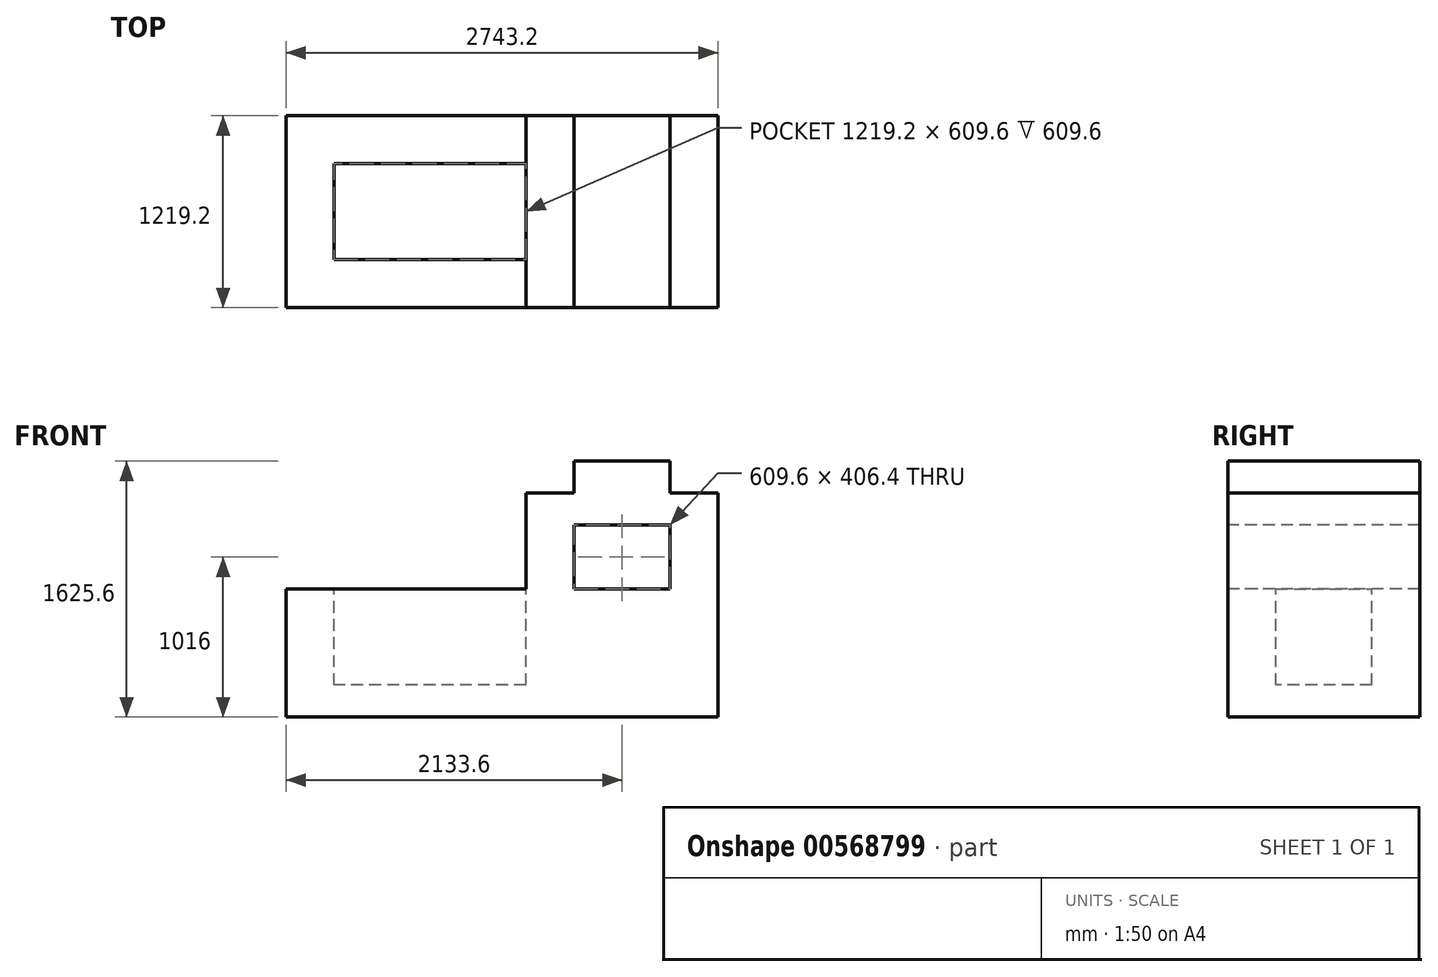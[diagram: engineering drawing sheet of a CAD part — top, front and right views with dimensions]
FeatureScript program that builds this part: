
annotation { "Feature Type Name" : "Feature", "Feature Type Description" : "" }
export const myFeature = defineFeature(function(context is Context, id is Id, definition is map)
    precondition{}
    {
        {
            var Q0;
            Q0=qCreatedBy(makeId("Front.planeOp"),FACE);
            var sketch = newSketch(context, id + "F0", { "sketchPlane" : qUnion([Q0])});
            skLineSegment(sketch, "E0.bottom", {"start": v(0, 0) * mm, "end": v(-2743.2, 0) * mm});
            skLineSegment(sketch, "E0.top", {"start": v(0, 1625.6) * mm, "end": v(-2743.2, 1625.6) * mm});
            skLineSegment(sketch, "E0.left", {"start": v(0, 0) * mm, "end": v(0, 1625.6) * mm});
            skLineSegment(sketch, "E0.right", {"start": v(-2743.2, 0) * mm, "end": v(-2743.2, 1625.6) * mm});
            skSolve(sketch);
        }
        {
            var Q0;
            Q0=makeQuery(id+"F0.imprint","IMPRINT",FACE,{"disambiguationData":[TD([[makeQuery(id+"F0.imprint","IMPRINT",EDGE,{"derivedFrom":sQuery(id+"F0.wireOp",EDGE,"E0.bottom")}),-1.0]])]});
            extrude(context, id + "F1", {"entities" : qUnion([Q0]), "depth" : 1219.2 * mm, "offsetDistance" : 25.4 * mm});
        }
        {
            var Q0;
            Q0=makeQuery(id+"F1.opExtrude","CAP_FACE",FACE,{"disambiguationData":[OSD([sQuery(id+"F0.wireOp",EDGE,"E0.bottom"),sQuery(id+"F0.wireOp",EDGE,"E0.top"),sQuery(id+"F0.wireOp",EDGE,"E0.left"),sQuery(id+"F0.wireOp",EDGE,"E0.right")])],"isStart":false});
            var sketch = newSketch(context, id + "F2", { "sketchPlane" : qUnion([Q0])});
            skLineSegment(sketch, "E1.bottom", {"start": v(-2743.2, 1625.6) * mm, "end": v(-1219.2, 1625.6) * mm});
            skLineSegment(sketch, "E1.top", {"start": v(-2743.2, 812.8) * mm, "end": v(-1219.2, 812.8) * mm});
            skLineSegment(sketch, "E1.left", {"start": v(-2743.2, 1625.6) * mm, "end": v(-2743.2, 812.8) * mm});
            skLineSegment(sketch, "E1.right", {"start": v(-1219.2, 1625.6) * mm, "end": v(-1219.2, 812.8) * mm});
            skSolve(sketch);
        }
        {
            var Q0;
            Q0 = qSketchRegion(id + "F2", true);
            var Q1;
            Q1=makeQuery(id+"F2.imprint","IMPRINT",FACE,{"disambiguationData":[TD([[makeQuery(id+"F2.imprint","IMPRINT",EDGE,{"derivedFrom":sQuery(id+"F2.wireOp",EDGE,"E1.bottom")}),1.0]])]});
            extrude(context, id + "F3", {"entities" : qUnion([Q0, Q1]), "operationType" : NewBodyOperationType.REMOVE, "endBound" : BoundingType.THROUGH_ALL, "oppositeDirection" : true, "depth" : 25.4 * mm, "offsetDistance" : 25.4 * mm});
        }
        {
            var Q0;
            Q0=makeQuery(id+"F1.opExtrude","CAP_FACE",FACE,{"disambiguationData":[OSD([sQuery(id+"F0.wireOp",EDGE,"E0.bottom"),sQuery(id+"F0.wireOp",EDGE,"E0.top"),sQuery(id+"F0.wireOp",EDGE,"E0.left"),sQuery(id+"F0.wireOp",EDGE,"E0.right")])],"isStart":false});
            var sketch = newSketch(context, id + "F4", { "sketchPlane" : qUnion([Q0])});
            skLineSegment(sketch, "E2.bottom", {"start": v(-1219.2, 1625.6) * mm, "end": v(-914.4, 1625.6) * mm});
            skLineSegment(sketch, "E2.top", {"start": v(-1219.2, 1422.4) * mm, "end": v(-914.4, 1422.4) * mm});
            skLineSegment(sketch, "E2.left", {"start": v(-1219.2, 1625.6) * mm, "end": v(-1219.2, 1422.4) * mm});
            skLineSegment(sketch, "E2.right", {"start": v(-914.4, 1625.6) * mm, "end": v(-914.4, 1422.4) * mm});
            skSolve(sketch);
        }
        {
            var Q0;
            Q0 = qSketchRegion(id + "F4", true);
            extrude(context, id + "F5", {"entities" : qUnion([Q0]), "operationType" : NewBodyOperationType.REMOVE, "endBound" : BoundingType.THROUGH_ALL, "oppositeDirection" : true, "depth" : 25.4 * mm, "offsetDistance" : 25.4 * mm});
        }
        {
            var Q0;
            Q0=makeQuery(id+"F1.opExtrude","CAP_FACE",FACE,{"disambiguationData":[OSD([sQuery(id+"F0.wireOp",EDGE,"E0.bottom"),sQuery(id+"F0.wireOp",EDGE,"E0.top"),sQuery(id+"F0.wireOp",EDGE,"E0.left"),sQuery(id+"F0.wireOp",EDGE,"E0.right")])],"isStart":false});
            var sketch = newSketch(context, id + "F6", { "sketchPlane" : qUnion([Q0])});
            skLineSegment(sketch, "E3.bottom", {"start": v(0, 1625.6) * mm, "end": v(-304.8, 1625.6) * mm});
            skLineSegment(sketch, "E3.top", {"start": v(0, 1422.4) * mm, "end": v(-304.8, 1422.4) * mm});
            skLineSegment(sketch, "E3.left", {"start": v(0, 1625.6) * mm, "end": v(0, 1422.4) * mm});
            skLineSegment(sketch, "E3.right", {"start": v(-304.8, 1625.6) * mm, "end": v(-304.8, 1422.4) * mm});
            skSolve(sketch);
        }
        {
            var Q0;
            Q0 = qSketchRegion(id + "F6", true);
            extrude(context, id + "F7", {"entities" : qUnion([Q0]), "operationType" : NewBodyOperationType.REMOVE, "endBound" : BoundingType.THROUGH_ALL, "oppositeDirection" : true, "depth" : 25.4 * mm, "offsetDistance" : 25.4 * mm});
        }
        {
            var Q0;
            Q0=makeQuery(id+"F1.opExtrude","CAP_FACE",FACE,{"disambiguationData":[OSD([sQuery(id+"F0.wireOp",EDGE,"E0.bottom"),sQuery(id+"F0.wireOp",EDGE,"E0.top"),sQuery(id+"F0.wireOp",EDGE,"E0.left"),sQuery(id+"F0.wireOp",EDGE,"E0.right")])],"isStart":false});
            var sketch = newSketch(context, id + "F8", { "sketchPlane" : qUnion([Q0])});
            skLineSegment(sketch, "E4", {"start": v(-1219.2, 1422.4) * mm, "end": v(-1219.2, 1219.2) * mm});
            skLineSegment(sketch, "E5.bottom", {"start": v(-914.4, 1219.2) * mm, "end": v(-304.8, 1219.2) * mm});
            skLineSegment(sketch, "E5.top", {"start": v(-914.4, 812.8) * mm, "end": v(-304.8, 812.8) * mm});
            skLineSegment(sketch, "E5.left", {"start": v(-914.4, 1219.2) * mm, "end": v(-914.4, 812.8) * mm});
            skLineSegment(sketch, "E5.right", {"start": v(-304.8, 1219.2) * mm, "end": v(-304.8, 812.8) * mm});
            skSolve(sketch);
        }
        {
            var Q0;
            Q0=makeQuery(id+"F8.imprint","IMPRINT",FACE,{"disambiguationData":[TD([[makeQuery(id+"F8.imprint","IMPRINT",EDGE,{"derivedFrom":sQuery(id+"F8.wireOp",EDGE,"E5.bottom")}),-1.0]])]});
            extrude(context, id + "F9", {"entities" : qUnion([Q0]), "operationType" : NewBodyOperationType.REMOVE, "endBound" : BoundingType.THROUGH_ALL, "oppositeDirection" : true, "depth" : 25.4 * mm, "offsetDistance" : 25.4 * mm});
        }
        {
            var Q0;
            Q0=makeQuery(id+"F3.boolean.opBoolean","COPY",FACE,{"derivedFrom":makeQuery(id+"F3.opExtrude","SWEPT_FACE",FACE,{"disambiguationData":[OSD([sQuery(id+"F2.wireOp",EDGE,"E1.top")])]})});
            var sketch = newSketch(context, id + "F10", { "sketchPlane" : qUnion([Q0])});
            skLineSegment(sketch, "E6", {"start": v(-1219.2, -1219.2) * mm, "end": v(-1219.2, -914.4) * mm});
            skLineSegment(sketch, "E7.bottom", {"start": v(-1219.2, -914.4) * mm, "end": v(-2438.4, -914.4) * mm});
            skLineSegment(sketch, "E7.top", {"start": v(-1219.2, -304.8) * mm, "end": v(-2438.4, -304.8) * mm});
            skLineSegment(sketch, "E7.left", {"start": v(-1219.2, -914.4) * mm, "end": v(-1219.2, -304.8) * mm});
            skLineSegment(sketch, "E7.right", {"start": v(-2438.4, -914.4) * mm, "end": v(-2438.4, -304.8) * mm});
            skSolve(sketch);
        }
        {
            var Q0;
            Q0 = qSketchRegion(id + "F10", true);
            extrude(context, id + "F11", {"entities" : qUnion([Q0]), "operationType" : NewBodyOperationType.REMOVE, "oppositeDirection" : true, "depth" : 609.6 * mm, "offsetDistance" : 25.4 * mm});
        }
    });
